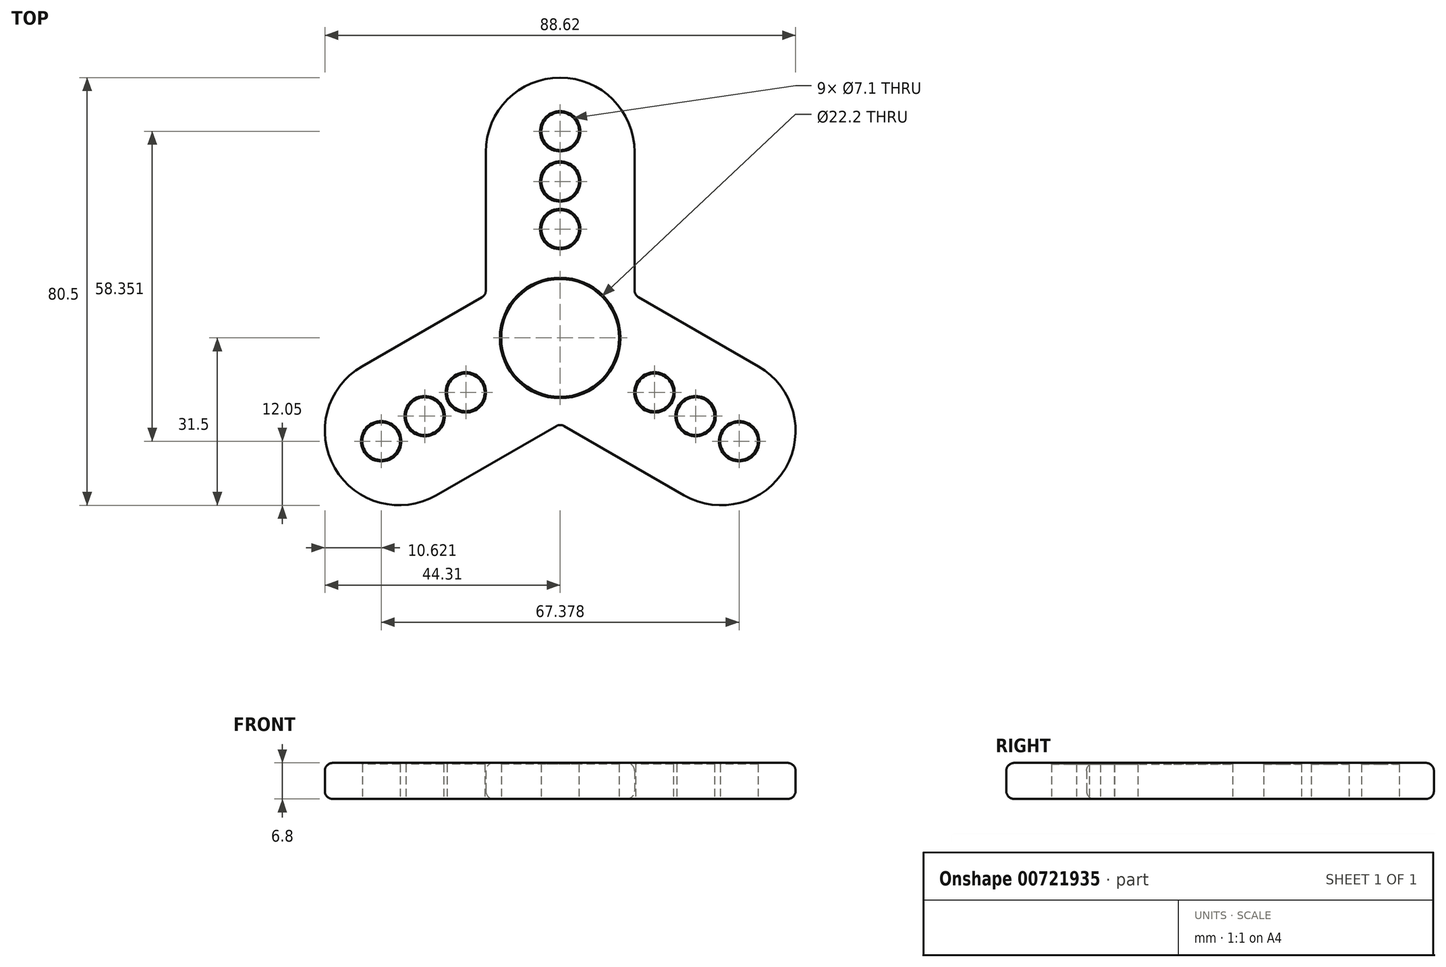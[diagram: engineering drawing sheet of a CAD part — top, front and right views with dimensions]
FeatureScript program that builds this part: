
annotation { "Feature Type Name" : "Feature", "Feature Type Description" : "" }
export const myFeature = defineFeature(function(context is Context, id is Id, definition is map)
    precondition{}
    {
        {
            var Q0;
            Q0=qCreatedBy(makeId("Top.planeOp"),FACE);
            var Q1;
            Q1=qCreatedBy(makeId("Top.planeOp"),FACE);
            var sketch = newSketch(context, id + "F0", { "sketchPlane" : qUnion([Q0, Q1])});
            skCircle(sketch, "E0", {"center": v(0, 0) * mm, "radius": 11.1 * mm});
            skCircle(sketch, "E1", {"center": v(0, 0) * mm, "radius": 14 * mm});
            skCircle(sketch, "E2", {"center": v(0, 29.45) * mm, "radius": 3.55 * mm});
            skCircle(sketch, "E3", {"center": v(0, 20.5) * mm, "radius": 3.55 * mm});
            skLineSegment(sketch, "E4", {"start": v(-14, 0) * mm, "end": v(-14, 35) * mm});
            skLineSegment(sketch, "E5", {"start": v(14, 0) * mm, "end": v(14, 35) * mm});
            skCircle(sketch, "E6", {"center": v(0, 35) * mm, "radius": 14 * mm});
            skCircle(sketch, "E7.1.0", {"center": v(-30.31, -17.5) * mm, "radius": 14 * mm});
            skCircle(sketch, "E7.2.0", {"center": v(30.31, -17.5) * mm, "radius": 14 * mm});
            skLineSegment(sketch, "E8.1.0", {"start": v(7, -12.12) * mm, "end": v(-23.31, -29.62) * mm});
            skLineSegment(sketch, "E8.2.0", {"start": v(7, 12.12) * mm, "end": v(37.31, -5.38) * mm});
            skLineSegment(sketch, "E9.1.0", {"start": v(-7, 12.12) * mm, "end": v(-37.31, -5.38) * mm});
            skLineSegment(sketch, "E9.2.0", {"start": v(-7, -12.12) * mm, "end": v(23.31, -29.62) * mm});
            skCircle(sketch, "E10.1.0", {"center": v(-25.5, -14.72) * mm, "radius": 3.55 * mm});
            skCircle(sketch, "E10.2.0", {"center": v(25.5, -14.72) * mm, "radius": 3.55 * mm});
            skCircle(sketch, "E11.1.0", {"center": v(-17.76, -10.25) * mm, "radius": 3.55 * mm});
            skCircle(sketch, "E11.2.0", {"center": v(17.76, -10.25) * mm, "radius": 3.55 * mm});
            skCircle(sketch, "E12", {"center": v(0, 38.9) * mm, "radius": 3.55 * mm});
            skCircle(sketch, "E13.1.0", {"center": v(-33.69, -19.45) * mm, "radius": 3.55 * mm});
            skCircle(sketch, "E13.2.0", {"center": v(33.69, -19.45) * mm, "radius": 3.55 * mm});
            skSolve(sketch);
        }
        {
            var Q0;
            {var subQ0=sQuery(id+"F0.wireOp",EDGE,"E4");var subQ1=sQuery(id+"F0.wireOp",EDGE,"E1");var subQ2=makeQuery(id+"F0.imprint","INTERSECT",VERTEX,{"derivedFrom":[subQ1,subQ0]});Q0=makeQuery(id+"F0.imprint","IMPRINT",FACE,{"disambiguationData":[TD([[makeQuery(id+"F0.imprint","IMPRINT",EDGE,{"disambiguationData":[TD([[subQ2,1.0]])],"derivedFrom":subQ1}),-1.0]])]});}
            var Q1;
            {var subQ3=sQuery(id+"F0.wireOp",EDGE,"E8.2.0");var subQ5=sQuery(id+"F0.wireOp",EDGE,"E1");var subQ6=makeQuery(id+"F0.imprint","INTERSECT",VERTEX,{"derivedFrom":[subQ5,subQ3]});Q1=makeQuery(id+"F0.imprint","IMPRINT",FACE,{"disambiguationData":[TD([[makeQuery(id+"F0.imprint","IMPRINT",EDGE,{"disambiguationData":[TD([[subQ6,-1.0]])],"derivedFrom":subQ5}),-1.0]])]});}
            var Q2;
            Q2=makeQuery(id+"F0.imprint","IMPRINT",FACE,{"disambiguationData":[TD([[makeQuery(id+"F0.imprint","IMPRINT",EDGE,{"derivedFrom":sQuery(id+"F0.wireOp",EDGE,"E2")}),-1.0]])]});
            var Q3;
            {var subQ8=sQuery(id+"F0.wireOp",EDGE,"E5");var subQ9=sQuery(id+"F0.wireOp",EDGE,"E1");var subQ10=makeQuery(id+"F0.imprint","INTERSECT",VERTEX,{"derivedFrom":[subQ9,subQ8]});Q3=makeQuery(id+"F0.imprint","IMPRINT",FACE,{"disambiguationData":[TD([[makeQuery(id+"F0.imprint","IMPRINT",EDGE,{"disambiguationData":[TD([[subQ10,1.0]])],"derivedFrom":subQ9}),-1.0]])]});}
            var Q4;
            Q4=makeQuery(id+"F0.imprint","IMPRINT",FACE,{"disambiguationData":[TD([[makeQuery(id+"F0.imprint","IMPRINT",EDGE,{"derivedFrom":sQuery(id+"F0.wireOp",EDGE,"E10.2.0")}),-1.0]])]});
            var Q5;
            Q5=makeQuery(id+"F0.imprint","IMPRINT",FACE,{"disambiguationData":[TD([[makeQuery(id+"F0.imprint","IMPRINT",EDGE,{"derivedFrom":sQuery(id+"F0.wireOp",EDGE,"E10.1.0")}),-1.0]])]});
            var Q6;
            {var subQ5=sQuery(id+"F0.wireOp",EDGE,"E4");var subQ6=sQuery(id+"F0.wireOp",EDGE,"E1");var subQ7=makeQuery(id+"F0.imprint","INTERSECT",VERTEX,{"derivedFrom":[subQ6,subQ5]});Q6=makeQuery(id+"F0.imprint","IMPRINT",FACE,{"disambiguationData":[TD([[makeQuery(id+"F0.imprint","IMPRINT",EDGE,{"disambiguationData":[TD([[subQ7,-1.0]])],"derivedFrom":subQ6}),-1.0]])]});}
            var Q7;
            {var subQ0=sQuery(id+"F0.wireOp",EDGE,"E8.1.0");var subQ1=sQuery(id+"F0.wireOp",EDGE,"E1");var subQ2=makeQuery(id+"F0.imprint","INTERSECT",VERTEX,{"derivedFrom":[subQ1,subQ0]});Q7=makeQuery(id+"F0.imprint","IMPRINT",FACE,{"disambiguationData":[TD([[makeQuery(id+"F0.imprint","IMPRINT",EDGE,{"disambiguationData":[TD([[subQ2,1.0]])],"derivedFrom":subQ1}),-1.0]])]});}
            var Q8;
            Q8=makeQuery(id+"F0.imprint","IMPRINT",FACE,{"disambiguationData":[TD([[makeQuery(id+"F0.imprint","IMPRINT",EDGE,{"derivedFrom":sQuery(id+"F0.wireOp",EDGE,"E0")}),-1.0]])]});
            var Q9;
            {var subQ0=sQuery(id+"F0.wireOp",EDGE,"E5");var subQ1=sQuery(id+"F0.wireOp",EDGE,"E1");var subQ2=makeQuery(id+"F0.imprint","INTERSECT",VERTEX,{"derivedFrom":[subQ1,subQ0]});Q9=makeQuery(id+"F0.imprint","IMPRINT",FACE,{"disambiguationData":[TD([[makeQuery(id+"F0.imprint","IMPRINT",EDGE,{"disambiguationData":[TD([[subQ2,-1.0]])],"derivedFrom":subQ1}),-1.0]])]});}
            extrude(context, id + "F1", {"entities" : qUnion([Q0, Q1, Q2, Q3, Q4, Q5, Q6, Q7, Q8, Q9]), "depth" : 6.8 * mm, "offsetDistance" : 25 * mm});
        }
        {
            var Q0;
            Q0=makeQuery(id+"F1.opExtrude","SWEPT_FACE",FACE,{"disambiguationData":[OSD([sQuery(id+"F0.wireOp",EDGE,"E7.1.0")])]});
            var Q1;
            Q1=makeQuery(id+"F1.opExtrude","SWEPT_FACE",FACE,{"disambiguationData":[OSD([sQuery(id+"F0.wireOp",EDGE,"E8.1.0")])]});
            var Q2;
            Q2=makeQuery(id+"F1.opExtrude","SWEPT_FACE",FACE,{"disambiguationData":[OSD([sQuery(id+"F0.wireOp",EDGE,"E9.2.0")])]});
            var Q3;
            Q3=makeQuery(id+"F1.opExtrude","SWEPT_FACE",FACE,{"disambiguationData":[OSD([sQuery(id+"F0.wireOp",EDGE,"E7.2.0")])]});
            var Q4;
            Q4=makeQuery(id+"F1.opExtrude","SWEPT_FACE",FACE,{"disambiguationData":[OSD([sQuery(id+"F0.wireOp",EDGE,"E8.2.0")])]});
            var Q5;
            Q5=makeQuery(id+"F1.opExtrude","SWEPT_FACE",FACE,{"disambiguationData":[OSD([sQuery(id+"F0.wireOp",EDGE,"E5")])]});
            var Q6;
            Q6=makeQuery(id+"F1.opExtrude","SWEPT_FACE",FACE,{"disambiguationData":[OSD([sQuery(id+"F0.wireOp",EDGE,"E6")])]});
            var Q7;
            Q7=makeQuery(id+"F1.opExtrude","SWEPT_FACE",FACE,{"disambiguationData":[OSD([sQuery(id+"F0.wireOp",EDGE,"E4")])]});
            var Q8;
            Q8=makeQuery(id+"F1.opExtrude","SWEPT_FACE",FACE,{"disambiguationData":[OSD([sQuery(id+"F0.wireOp",EDGE,"E9.1.0")])]});
            fillet(context, id + "F2", {"entities" : qUnion([Q0, Q1, Q2, Q3, Q4, Q5, Q6, Q7, Q8]), "radius" : 1.5 * mm, "tangentPropagation" : true, "allowEdgeOverflow" : false});
        }
        {
            var Q0;
            Q0=makeQuery(id+"F1.opExtrude","CAP_EDGE",EDGE,{"disambiguationData":[OSD([sQuery(id+"F0.wireOp",EDGE,"E13.1.0")])],"isStart":false});
            var Q1;
            Q1=makeQuery(id+"F1.opExtrude","CAP_EDGE",EDGE,{"disambiguationData":[OSD([sQuery(id+"F0.wireOp",EDGE,"E10.1.0")])],"isStart":false});
            var Q2;
            Q2=makeQuery(id+"F1.opExtrude","CAP_EDGE",EDGE,{"disambiguationData":[OSD([sQuery(id+"F0.wireOp",EDGE,"E11.1.0")])],"isStart":false});
            var Q3;
            Q3=makeQuery(id+"F1.opExtrude","CAP_EDGE",EDGE,{"disambiguationData":[OSD([sQuery(id+"F0.wireOp",EDGE,"E0")])],"isStart":false});
            var Q4;
            Q4=makeQuery(id+"F1.opExtrude","CAP_EDGE",EDGE,{"disambiguationData":[OSD([sQuery(id+"F0.wireOp",EDGE,"E3")])],"isStart":false});
            var Q5;
            Q5=makeQuery(id+"F1.opExtrude","CAP_EDGE",EDGE,{"disambiguationData":[OSD([sQuery(id+"F0.wireOp",EDGE,"E2")])],"isStart":false});
            var Q6;
            Q6=makeQuery(id+"F1.opExtrude","CAP_EDGE",EDGE,{"disambiguationData":[OSD([sQuery(id+"F0.wireOp",EDGE,"E12")])],"isStart":false});
            var Q7;
            Q7=makeQuery(id+"F1.opExtrude","CAP_EDGE",EDGE,{"disambiguationData":[OSD([sQuery(id+"F0.wireOp",EDGE,"E11.2.0")])],"isStart":false});
            var Q8;
            Q8=makeQuery(id+"F1.opExtrude","CAP_EDGE",EDGE,{"disambiguationData":[OSD([sQuery(id+"F0.wireOp",EDGE,"E10.2.0")])],"isStart":false});
            var Q9;
            Q9=makeQuery(id+"F1.opExtrude","CAP_EDGE",EDGE,{"disambiguationData":[OSD([sQuery(id+"F0.wireOp",EDGE,"E13.2.0")])],"isStart":false});
            chamfer(context, id + "F3", {"entities" : qUnion([Q0, Q1, Q2, Q3, Q4, Q5, Q6, Q7, Q8, Q9]), "width" : 0.25 * mm, "tangentPropagation" : true});
        }
    });
